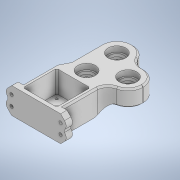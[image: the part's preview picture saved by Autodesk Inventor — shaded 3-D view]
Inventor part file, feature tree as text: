
AUTODESK INVENTOR PART (.ipt)
format: ipt  version: 2021 (Build 250183000, 183)  size: 489,472 bytes
history: native  units: mm
features: extrude x11, sketch x11, chamfer x7, fillet x3, plane x2
ambient origin geometry x8: Origin, YZ Plane, XZ Plane, XY Plane, X Axis, Y Axis, Z Axis, Center Point
bodies: Solid1 (feature_tree)
feature tree (34):
  extrude  "Extrusion1"  Depth=22.4mm
  plane  "Work Plane1"
  extrude  "Extrusion3"  Depth=38.5mm
  extrude  "Extrusion4"  Depth=40.0mm
  chamfer  "Chamfer2"  Distance=21.0mm
  extrude  "Extrusion2"  Depth=14.0mm
  extrude  "Extrusion5"  Depth=7.0mm TaperAngle=0.0deg
  extrude  "Extrusion6"  Depth=42.2mm
  chamfer  "Chamfer3"  Distance=5.0mm
  chamfer  "Chamfer4"  Distance=7.0mm
  chamfer  "Chamfer5"  Distance=3.2mm
  extrude  "Extrusion7"  Depth=3.2mm
  plane  "Work Plane2"
  extrude  "Extrusion8"  Depth=3.2mm
  chamfer  "Chamfer7"  Distance=3.2mm
  fillet  "Fillet1"  Radius=31.5mm
  extrude  "Extrusion10"  Depth=31.5mm
  chamfer  "Chamfer10"  Distance=31.5mm
  extrude  "Extrusion11"  Depth=31.5mm
  extrude  "Extrusion12"  Depth=5.35mm
  fillet  "Fillet2"  Radius=5.35mm
  fillet  "Fillet3"  Radius=5.35mm
  chamfer  "Chamfer11"  Distance=5.35mm
  sketch  "Sketch1"  dims[d0=22.4mm d1=22.4mm]
  sketch  "Sketch2"  dims[d2=0.0mm d3=38.5mm]
  sketch  "Sketch3"  dims[d4=40.0mm d5=40.0mm d6=21.0mm d7=0.0mm]
  sketch  "Sketch4"  dims[d8=-7.0mm d9=14.0mm]
  sketch  "Sketch5"  dims[d10=14.0mm d11=7.0mm d12=0.0mm]
  sketch  "Sketch6"  dims[d16=42.2mm d17=42.2mm]
  sketch  "Sketch8"  dims[d18=21.1mm]
  sketch  "Sketch9"  dims[d19=21.1mm]
  sketch  "Sketch11"  dims[d20=23.0mm]
  sketch  "Sketch12"  dims[d21=0.0mm]
  sketch  "Sketch13"  dims[d22=38.0mm d23=5.0mm d24=7.0mm d25=0.0mm d26=3.2mm d27=3.2mm d28=3.2mm d29=3.2mm d30=31.5mm d31=31.5mm d32=31.5mm d33=31.5mm d34=5.35mm d35=5.35mm d36=5.35mm d37=5.35mm d38=23.0mm d39=21.1mm d40=21.1mm d41=5.0mm d42=0.0mm d43=11.9mm d44=2.0mm d45=45.0deg d47=4.2mm d48=4.2mm d52=10.0mm d54=4.2mm d55=4.2mm d59=10.0mm d60=8.0mm d61=0.0mm d62=10.0mm d63=10.0mm d64=10.0mm d65=10.0mm d66=4.0mm d67=0.0mm d68=5.0mm d69=2.0mm d70=45.0deg d71=2.0mm d72=2.0mm d73=45.0deg d74=0.1mm d75=2.0mm d76=45.0deg d80=22.4mm d83=19.0mm d84=19.0mm d85=10.0mm d86=0.0mm d87=38.5mm d88=38.5mm d89=-7.0mm d90=14.0mm d91=7.0mm d92=0.0mm d93=2.0mm d94=2.0mm d95=45.0deg d96=19.0mm d105=0.25mm d106=0.25mm d107=0.25mm d108=0.25mm d109=7.0mm d110=0.0mm d111=2.0mm d112=2.0mm d113=45.0deg d114=7.0mm d115=0.0mm d116=10.2mm d117=10.2mm d118=10.2mm d119=10.2mm d120=7.0mm d121=0.0mm d122=15.0mm d125=15.0mm d126=2.0mm d127=2.0mm d128=45.0deg]
